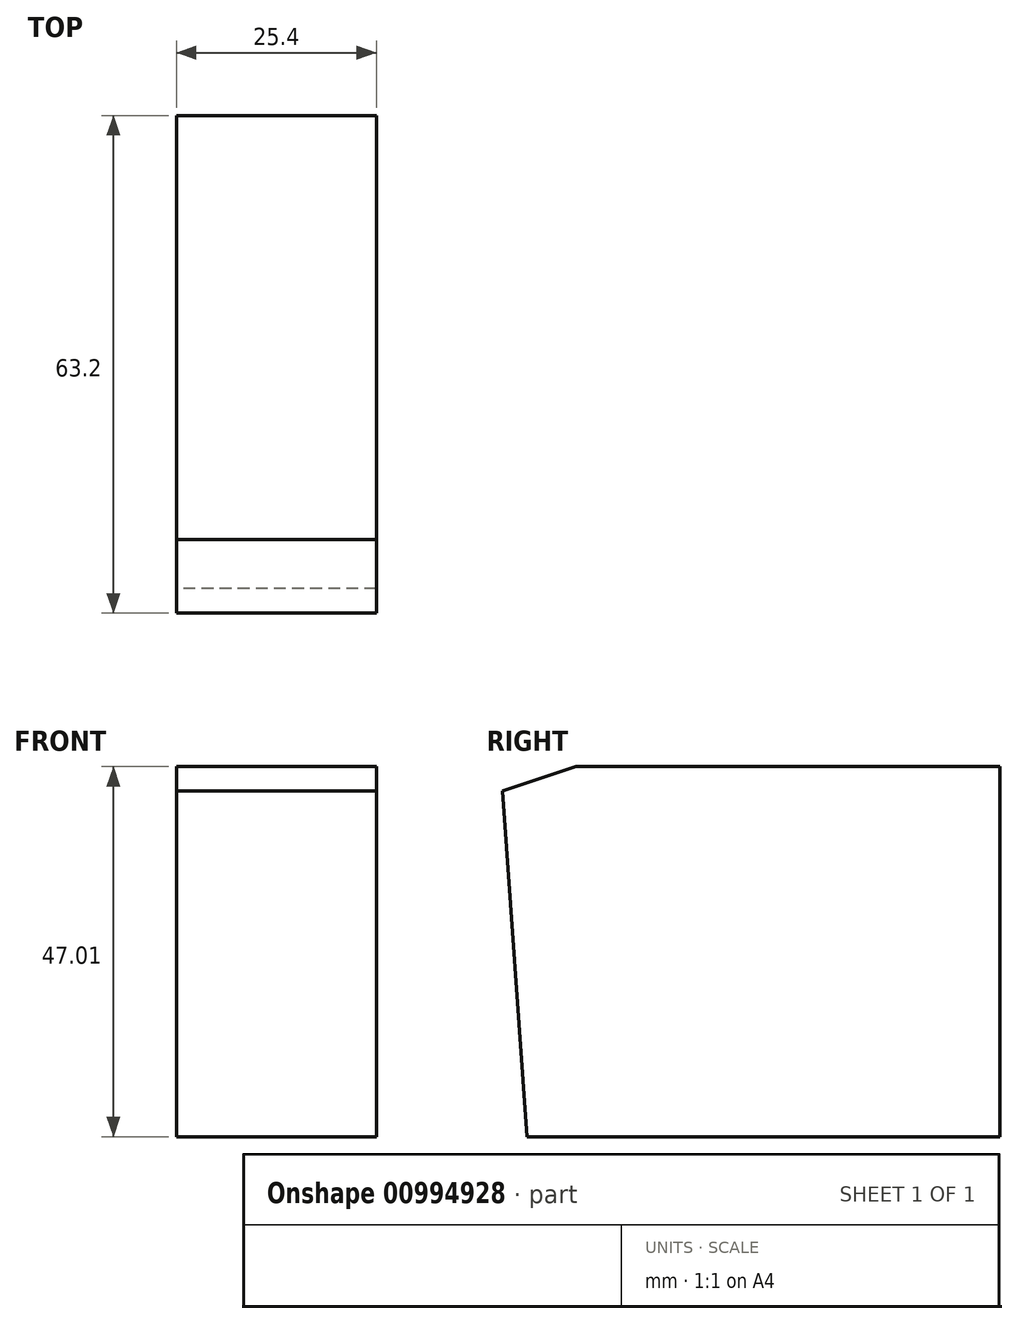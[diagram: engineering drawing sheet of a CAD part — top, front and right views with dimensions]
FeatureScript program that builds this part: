
annotation { "Feature Type Name" : "Feature", "Feature Type Description" : "" }
export const myFeature = defineFeature(function(context is Context, id is Id, definition is map)
    precondition{}
    {
        {
            var Q0;
            Q0=qCreatedBy(makeId("Right.planeOp"),FACE);
            var sketch = newSketch(context, id + "F0", { "sketchPlane" : qUnion([Q0])});
            skLineSegment(sketch, "E0", {"start": v(-38.76, 22.88) * mm, "end": v(-35.65, -21.01) * mm});
            skLineSegment(sketch, "E1", {"start": v(-35.65, -21.01) * mm, "end": v(24.44, -21.01) * mm});
            skLineSegment(sketch, "E2", {"start": v(24.44, -21.01) * mm, "end": v(24.44, 26) * mm});
            skLineSegment(sketch, "E3", {"start": v(24.44, 26) * mm, "end": v(-29.42, 26) * mm});
            skLineSegment(sketch, "E4", {"start": v(-29.42, 26) * mm, "end": v(-38.76, 22.88) * mm});
            skSolve(sketch);
        }
        {
            var Q0;
            Q0=makeQuery(id+"F0.imprint","IMPRINT",FACE,{"disambiguationData":[TD([[makeQuery(id+"F0.imprint","IMPRINT",EDGE,{"derivedFrom":sQuery(id+"F0.wireOp",EDGE,"E0")}),1.0]])]});
            extrude(context, id + "F1", {"entities" : qUnion([Q0]), "depth" : 25.4 * mm, "offsetDistance" : 25.4 * mm});
        }
    });
